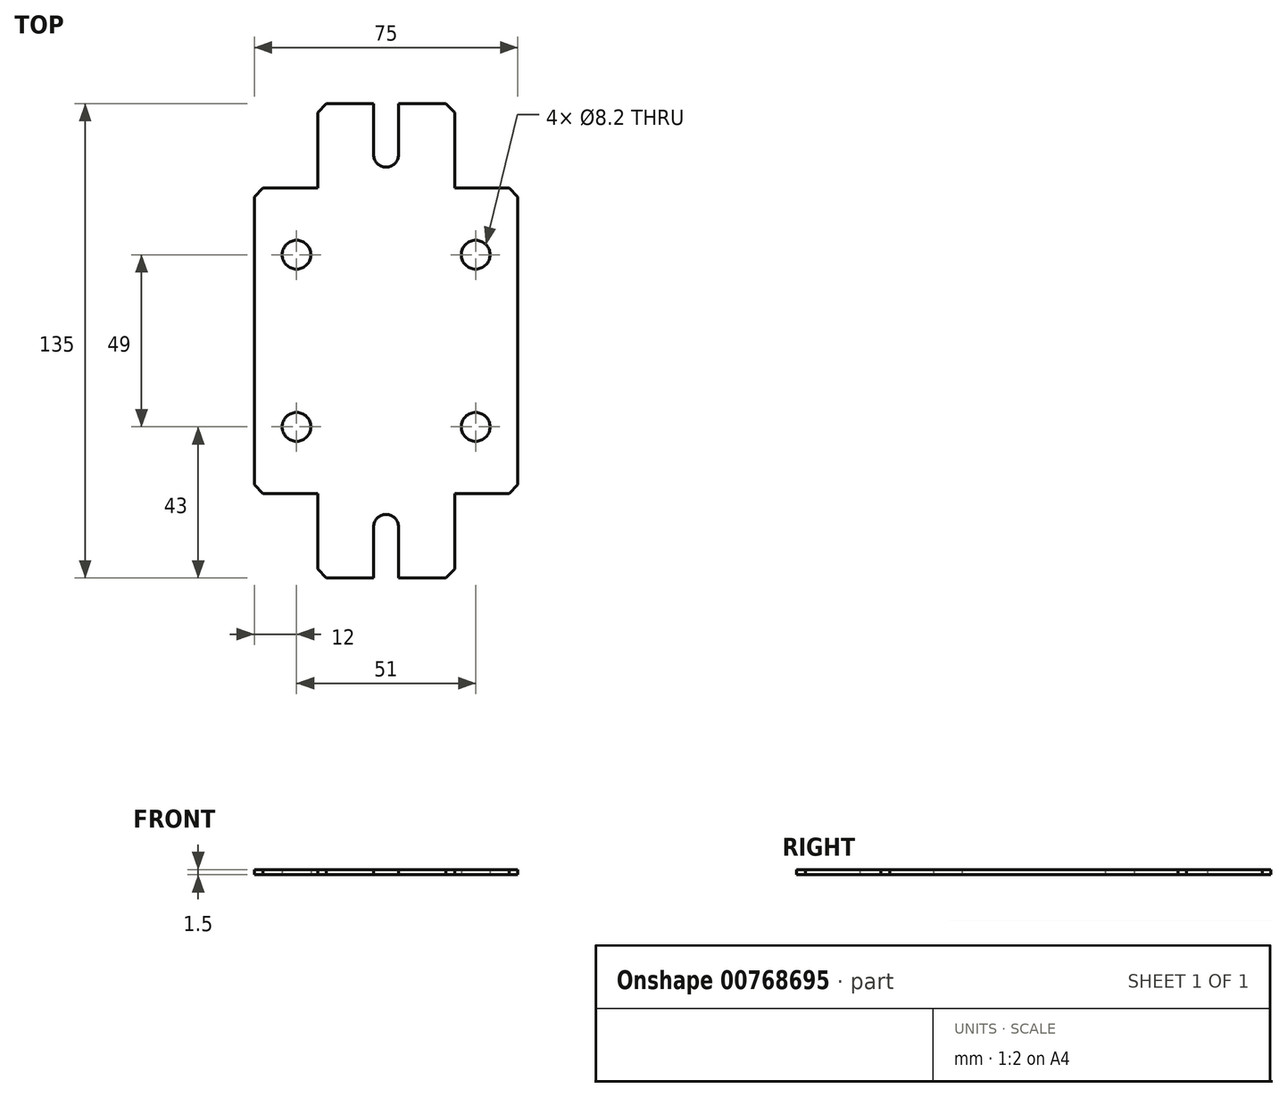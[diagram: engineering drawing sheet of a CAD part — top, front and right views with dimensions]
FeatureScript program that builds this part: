
annotation { "Feature Type Name" : "Feature", "Feature Type Description" : "" }
export const myFeature = defineFeature(function(context is Context, id is Id, definition is map)
    precondition{}
    {
        {
            var Q0;
            Q0=qCreatedBy(makeId("Top.planeOp"),FACE);
            var sketch = newSketch(context, id + "F0", { "sketchPlane" : qUnion([Q0])});
            skLineSegment(sketch, "E0.bottom", {"start": v(37.5, -67.5) * mm, "end": v(-37.5, -67.5) * mm});
            skLineSegment(sketch, "E0.top", {"start": v(37.5, 67.5) * mm, "end": v(-37.5, 67.5) * mm});
            skLineSegment(sketch, "E0.left", {"start": v(37.5, -67.5) * mm, "end": v(37.5, 67.5) * mm});
            skLineSegment(sketch, "E0.right", {"start": v(-37.5, -67.5) * mm, "end": v(-37.5, 67.5) * mm});
            skPoint(sketch, "E0.middle", {"position": v(0, 0) * mm});
            skLineSegment(sketch, "E1.bottom", {"start": v(-37.5, 67.5) * mm, "end": v(-19.5, 67.5) * mm});
            skLineSegment(sketch, "E1.top", {"start": v(-37.5, 43.5) * mm, "end": v(-19.5, 43.5) * mm});
            skLineSegment(sketch, "E1.left", {"start": v(-37.5, 67.5) * mm, "end": v(-37.5, 43.5) * mm});
            skLineSegment(sketch, "E1.right", {"start": v(-19.5, 67.5) * mm, "end": v(-19.5, 43.5) * mm});
            skCircle(sketch, "E2", {"center": v(-25.5, 24.5) * mm, "radius": 4.1 * mm});
            skLineSegment(sketch, "E3.MirrorCS", {"start": v(19.5, 67.5) * mm, "end": v(19.5, 43.5) * mm});
            skLineSegment(sketch, "E4.MirrorCS", {"start": v(37.5, 67.5) * mm, "end": v(37.5, 43.5) * mm});
            skLineSegment(sketch, "E5.MirrorCS", {"start": v(37.5, 67.5) * mm, "end": v(19.5, 67.5) * mm});
            skLineSegment(sketch, "E6.MirrorCS", {"start": v(37.5, 43.5) * mm, "end": v(19.5, 43.5) * mm});
            skCircle(sketch, "E7.MirrorC", {"center": v(25.5, 24.5) * mm, "radius": 4.1 * mm});
            skCircle(sketch, "E8", {"center": v(0, 53) * mm, "radius": 3.55 * mm});
            skLineSegment(sketch, "E9", {"start": v(3.55, 53) * mm, "end": v(3.55, 67.5) * mm});
            skLineSegment(sketch, "E10", {"start": v(-3.55, 53) * mm, "end": v(-3.55, 67.5) * mm});
            skLineSegment(sketch, "E11.MirrorCS", {"start": v(37.5, -67.5) * mm, "end": v(19.5, -67.5) * mm});
            skCircle(sketch, "E12.MirrorC", {"center": v(0, -53) * mm, "radius": 3.55 * mm});
            skLineSegment(sketch, "E13.MirrorCS", {"start": v(-3.55, -53) * mm, "end": v(-3.55, -67.5) * mm});
            skLineSegment(sketch, "E14.MirrorCS", {"start": v(37.5, -67.5) * mm, "end": v(37.5, -43.5) * mm});
            skLineSegment(sketch, "E15.MirrorCS", {"start": v(19.5, -67.5) * mm, "end": v(19.5, -43.5) * mm});
            skLineSegment(sketch, "E16.MirrorCS", {"start": v(-19.5, -67.5) * mm, "end": v(-19.5, -43.5) * mm});
            skCircle(sketch, "E17.MirrorC", {"center": v(25.5, -24.5) * mm, "radius": 4.1 * mm});
            skLineSegment(sketch, "E18.MirrorCS", {"start": v(-37.5, -67.5) * mm, "end": v(-37.5, -43.5) * mm});
            skLineSegment(sketch, "E19.MirrorCS", {"start": v(37.5, -43.5) * mm, "end": v(19.5, -43.5) * mm});
            skLineSegment(sketch, "E20.MirrorCS", {"start": v(-37.5, -43.5) * mm, "end": v(-19.5, -43.5) * mm});
            skLineSegment(sketch, "E21.MirrorCS", {"start": v(-37.5, -67.5) * mm, "end": v(-19.5, -67.5) * mm});
            skCircle(sketch, "E22.MirrorC", {"center": v(-25.5, -24.5) * mm, "radius": 4.1 * mm});
            skLineSegment(sketch, "E23.MirrorCS", {"start": v(3.55, -53) * mm, "end": v(3.55, -67.5) * mm});
            skSolve(sketch);
        }
        {
            var Q0;
            {var subQ16=sQuery(id+"F0.wireOp",EDGE,"E1.top");Q0=makeQuery(id+"F0.imprint","IMPRINT",FACE,{"disambiguationData":[TD([[makeQuery(id+"F0.imprint","IMPRINT",EDGE,{"derivedFrom":subQ16}),-1.0]])]});}
            extrude(context, id + "F1", {"entities" : qUnion([Q0]), "depth" : 1.5 * mm, "offsetDistance" : 25 * mm});
        }
        {
            var Q0;
            Q0=makeQuery(id+"F1.opExtrude","SWEPT_EDGE",EDGE,{"disambiguationData":[OSD([sQuery(id+"F0.wireOp",EDGE,"E0.right"),sQuery(id+"F0.wireOp",EDGE,"E1.top")])]});
            var Q1;
            Q1=makeQuery(id+"F1.opExtrude","SWEPT_EDGE",EDGE,{"disambiguationData":[OSD([sQuery(id+"F0.wireOp",EDGE,"E0.top"),sQuery(id+"F0.wireOp",EDGE,"E1.right")])]});
            var Q2;
            Q2=makeQuery(id+"F1.opExtrude","SWEPT_EDGE",EDGE,{"disambiguationData":[OSD([sQuery(id+"F0.wireOp",EDGE,"E0.top"),sQuery(id+"F0.wireOp",EDGE,"E3.MirrorCS")])]});
            var Q3;
            Q3=makeQuery(id+"F1.opExtrude","SWEPT_EDGE",EDGE,{"disambiguationData":[OSD([sQuery(id+"F0.wireOp",EDGE,"E0.left"),sQuery(id+"F0.wireOp",EDGE,"E6.MirrorCS")])]});
            var Q4;
            Q4=makeQuery(id+"F1.opExtrude","SWEPT_EDGE",EDGE,{"disambiguationData":[OSD([sQuery(id+"F0.wireOp",EDGE,"E0.right"),sQuery(id+"F0.wireOp",EDGE,"E20.MirrorCS")])]});
            var Q5;
            Q5=makeQuery(id+"F1.opExtrude","SWEPT_EDGE",EDGE,{"disambiguationData":[OSD([sQuery(id+"F0.wireOp",EDGE,"E0.bottom"),sQuery(id+"F0.wireOp",EDGE,"E16.MirrorCS")])]});
            var Q6;
            Q6=makeQuery(id+"F1.opExtrude","SWEPT_EDGE",EDGE,{"disambiguationData":[OSD([sQuery(id+"F0.wireOp",EDGE,"E0.bottom"),sQuery(id+"F0.wireOp",EDGE,"E15.MirrorCS")])]});
            var Q7;
            Q7=makeQuery(id+"F1.opExtrude","SWEPT_EDGE",EDGE,{"disambiguationData":[OSD([sQuery(id+"F0.wireOp",EDGE,"E0.left"),sQuery(id+"F0.wireOp",EDGE,"E19.MirrorCS")])]});
            chamfer(context, id + "F2", {"entities" : qUnion([Q0, Q1, Q2, Q3, Q4, Q5, Q6, Q7]), "width" : 2.5 * mm, "tangentPropagation" : true});
        }
    });
